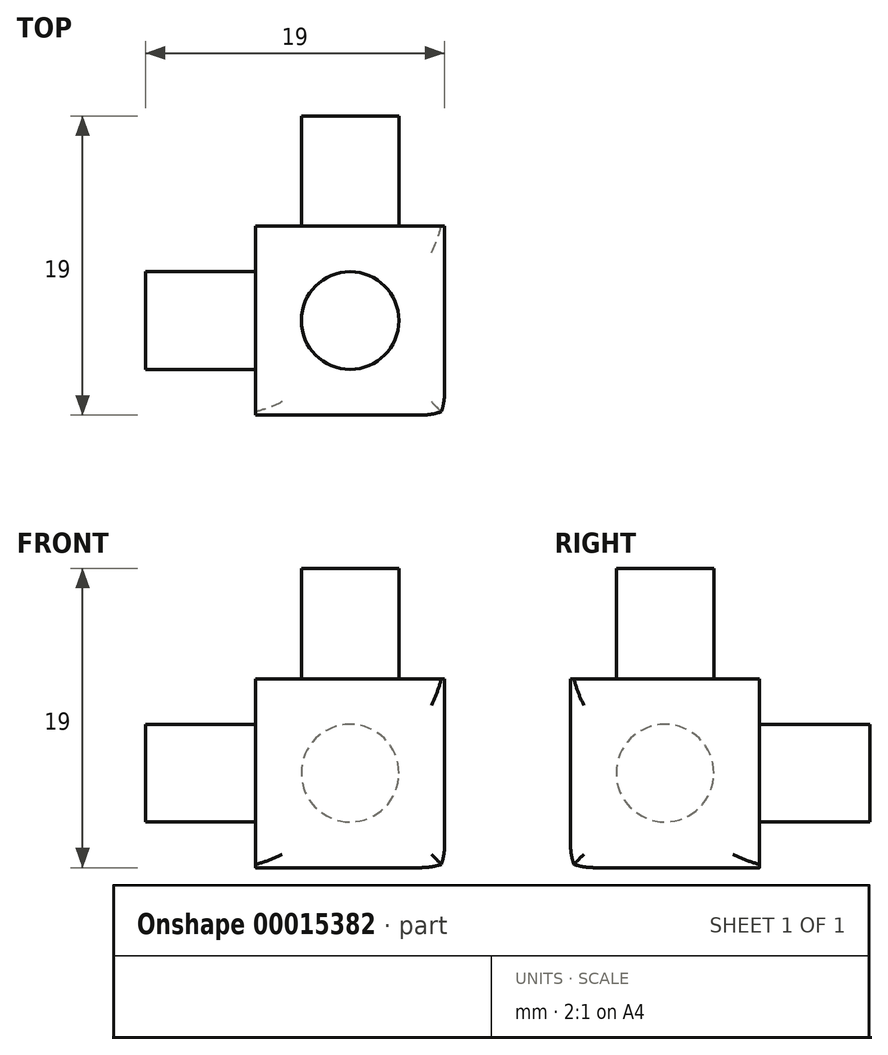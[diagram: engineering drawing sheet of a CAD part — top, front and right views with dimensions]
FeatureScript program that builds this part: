
annotation { "Feature Type Name" : "Feature", "Feature Type Description" : "" }
export const myFeature = defineFeature(function(context is Context, id is Id, definition is map)
    precondition{}
    {
        {
            var Q0;
            Q0=qCreatedBy(makeId("Top.planeOp"),FACE);
            var sketch = newSketch(context, id + "F0", { "sketchPlane" : qUnion([Q0])});
            skLineSegment(sketch, "E0.bottom", {"start": v(-6, 6) * mm, "end": v(6, 6) * mm});
            skLineSegment(sketch, "E0.top", {"start": v(-6, -6) * mm, "end": v(6, -6) * mm});
            skLineSegment(sketch, "E0.left", {"start": v(-6, 6) * mm, "end": v(-6, -6) * mm});
            skLineSegment(sketch, "E0.right", {"start": v(6, 6) * mm, "end": v(6, -6) * mm});
            skSolve(sketch);
        }
        {
            var Q0;
            Q0=makeQuery(id+"F0.imprint","IMPRINT",FACE,{"disambiguationData":[TD([[makeQuery(id+"F0.imprint","IMPRINT",EDGE,{"derivedFrom":sQuery(id+"F0.wireOp",EDGE,"E0.bottom")}),-1.0]])]});
            extrude(context, id + "F1", {"entities" : qUnion([Q0]), "depth" : 12 * mm});
        }
        {
            var Q0;
            Q0=makeQuery(id+"F1.opExtrude","CAP_VERTEX",VERTEX,{"disambiguationData":[OSD([sQuery(id+"F0.wireOp",EDGE,"E0.top"),sQuery(id+"F0.wireOp",EDGE,"E0.right")])],"isStart":false});
            var Q1;
            Q1=makeQuery(id+"F1.opExtrude","CAP_VERTEX",VERTEX,{"disambiguationData":[OSD([sQuery(id+"F0.wireOp",EDGE,"E0.top"),sQuery(id+"F0.wireOp",EDGE,"E0.left")])],"isStart":true});
            var Q2;
            Q2=makeQuery(id+"F1.opExtrude","CAP_VERTEX",VERTEX,{"disambiguationData":[OSD([sQuery(id+"F0.wireOp",EDGE,"E0.bottom"),sQuery(id+"F0.wireOp",EDGE,"E0.right")])],"isStart":true});
            cPlane(context, id + "F2", {"entities" : qUnion([Q0, Q1, Q2]), "cplaneType" : CPlaneType.THREE_POINT, "offset" : 150 * mm, "width" : 150 * mm, "height" : 150 * mm});
        }
        {
            var Q0;
            Q0=qCreatedBy(id+"F2.planeOp",FACE);
            var sketch = newSketch(context, id + "F3", { "sketchPlane" : qUnion([Q0])});
            skLineSegment(sketch, "E1.bottom", {"start": v(16.96, 18.13) * mm, "end": v(-15.43, 18.13) * mm});
            skLineSegment(sketch, "E1.top", {"start": v(16.96, -8.87) * mm, "end": v(-15.43, -8.87) * mm});
            skLineSegment(sketch, "E1.left", {"start": v(16.96, 18.13) * mm, "end": v(16.96, -8.87) * mm});
            skLineSegment(sketch, "E1.right", {"start": v(-15.43, 18.13) * mm, "end": v(-15.43, -8.87) * mm});
            skSolve(sketch);
        }
        {
            var Q0;
            Q0=makeQuery(id+"F3.imprint","IMPRINT",FACE,{"disambiguationData":[TD([[makeQuery(id+"F3.imprint","IMPRINT",EDGE,{"derivedFrom":sQuery(id+"F3.wireOp",EDGE,"E1.bottom")}),1.0]])]});
            extrude(context, id + "F4", {"entities" : qUnion([Q0]), "depth" : 25 * mm});
        }
        {
            var Q0;
            Q0=makeQuery(id+"F4.opExtrude","SWEPT_BODY",BODY,{"disambiguationData":[OSD([sQuery(id+"F3.wireOp",EDGE,"E1.bottom"),sQuery(id+"F3.wireOp",EDGE,"E1.top"),sQuery(id+"F3.wireOp",EDGE,"E1.left"),sQuery(id+"F3.wireOp",EDGE,"E1.right")])]});
            var Q1;
            Q1=makeQuery(id+"F1.opExtrude","SWEPT_BODY",BODY,{"disambiguationData":[OSD([sQuery(id+"F0.wireOp",EDGE,"E0.bottom"),sQuery(id+"F0.wireOp",EDGE,"E0.top"),sQuery(id+"F0.wireOp",EDGE,"E0.left"),sQuery(id+"F0.wireOp",EDGE,"E0.right")])]});
            booleanBodies(context, id + "F5", {"operationType" : BooleanOperationType.INTERSECTION, "tools" : qUnion([Q0, Q1])});
        }
        {
            var Q0;
            Q0=makeQuery(id+"F1.opExtrude","CAP_FACE",FACE,{"disambiguationData":[OSD([sQuery(id+"F0.wireOp",EDGE,"E0.bottom"),sQuery(id+"F0.wireOp",EDGE,"E0.top"),sQuery(id+"F0.wireOp",EDGE,"E0.left"),sQuery(id+"F0.wireOp",EDGE,"E0.right")])],"isStart":false});
            var sketch = newSketch(context, id + "F6", { "sketchPlane" : qUnion([Q0])});
            skCircle(sketch, "E2", {"center": v(0, 0) * mm, "radius": 3.1 * mm});
            skSolve(sketch);
        }
        {
            var Q0;
            Q0 = qSketchRegion(id + "F6", true);
            extrude(context, id + "F7", {"entities" : qUnion([Q0]), "operationType" : NewBodyOperationType.ADD, "depth" : 7 * mm});
        }
        {
            var Q0;
            Q0=makeQuery(id+"F1.opExtrude","SWEPT_FACE",FACE,{"disambiguationData":[OSD([sQuery(id+"F0.wireOp",EDGE,"E0.bottom")])]});
            var sketch = newSketch(context, id + "F8", { "sketchPlane" : qUnion([Q0])});
            skCircle(sketch, "E3", {"center": v(0, 6) * mm, "radius": 3.1 * mm});
            skSolve(sketch);
        }
        {
            var Q0;
            Q0 = qSketchRegion(id + "F8", true);
            extrude(context, id + "F9", {"entities" : qUnion([Q0]), "operationType" : NewBodyOperationType.ADD, "depth" : 7 * mm});
        }
        {
            var Q0;
            Q0=makeQuery(id+"F1.opExtrude","SWEPT_FACE",FACE,{"disambiguationData":[OSD([sQuery(id+"F0.wireOp",EDGE,"E0.left")])]});
            var sketch = newSketch(context, id + "F10", { "sketchPlane" : qUnion([Q0])});
            skCircle(sketch, "E4", {"center": v(0, 6) * mm, "radius": 3.1 * mm});
            skSolve(sketch);
        }
        {
            var Q0;
            Q0 = qSketchRegion(id + "F10", true);
            var Q1;
            Q1=sQuery(id+"F10.wireOp",EDGE,"E4");
            extrude(context, id + "F11", {"entities" : qUnion([Q0]), "operationType" : NewBodyOperationType.ADD, "surfaceEntities" : qUnion([Q1]), "depth" : 7 * mm});
        }
        {
            var Q0;
            Q0=makeQuery(id+"F4.opExtrude","CAP_FACE",FACE,{"disambiguationData":[OSD([sQuery(id+"F3.wireOp",EDGE,"E1.bottom"),sQuery(id+"F3.wireOp",EDGE,"E1.top"),sQuery(id+"F3.wireOp",EDGE,"E1.left"),sQuery(id+"F3.wireOp",EDGE,"E1.right")])],"isStart":true});
            fillet(context, id + "F12", {"entities" : qUnion([Q0]), "radius" : 2 * mm, "tangentPropagation" : true, "allowEdgeOverflow" : false});
        }
    });
